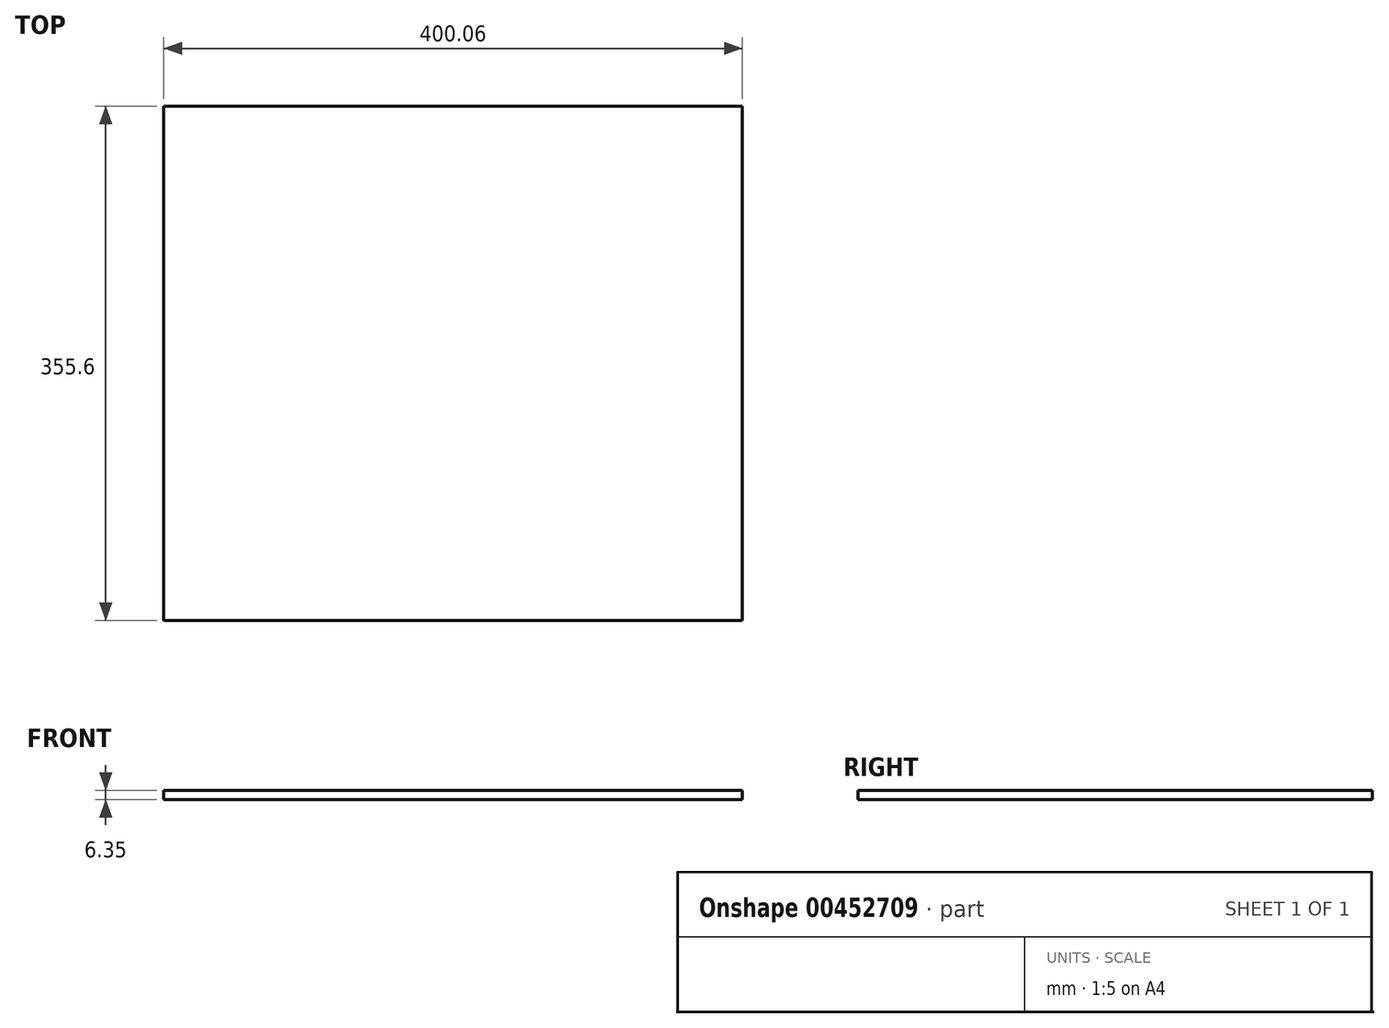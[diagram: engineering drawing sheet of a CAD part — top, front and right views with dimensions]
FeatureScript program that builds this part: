
annotation { "Feature Type Name" : "Feature", "Feature Type Description" : "" }
export const myFeature = defineFeature(function(context is Context, id is Id, definition is map)
    precondition{}
    {
        {
            var Q0;
            Q0=qCreatedBy(makeId("Top.planeOp"),FACE);
            var sketch = newSketch(context, id + "F0", { "sketchPlane" : qUnion([Q0])});
            skLineSegment(sketch, "E0.bottom", {"start": v(-200.02, 177.8) * mm, "end": v(200.03, 177.8) * mm});
            skLineSegment(sketch, "E0.top", {"start": v(-200.03, -177.8) * mm, "end": v(200.03, -177.8) * mm});
            skLineSegment(sketch, "E0.left", {"start": v(-200.02, 177.8) * mm, "end": v(-200.03, -177.8) * mm});
            skLineSegment(sketch, "E0.right", {"start": v(200.03, 177.8) * mm, "end": v(200.03, -177.8) * mm});
            skPoint(sketch, "E0.middle", {"position": v(0, 0) * mm});
            skSolve(sketch);
        }
        {
            var Q0;
            Q0=makeQuery(id+"F0.imprint","IMPRINT",FACE,{"disambiguationData":[TD([[makeQuery(id+"F0.imprint","IMPRINT",EDGE,{"derivedFrom":sQuery(id+"F0.wireOp",EDGE,"E0.bottom")}),-1.0]])]});
            extrude(context, id + "F1", {"entities" : qUnion([Q0]), "depth" : 6.35 * mm});
        }
    });
